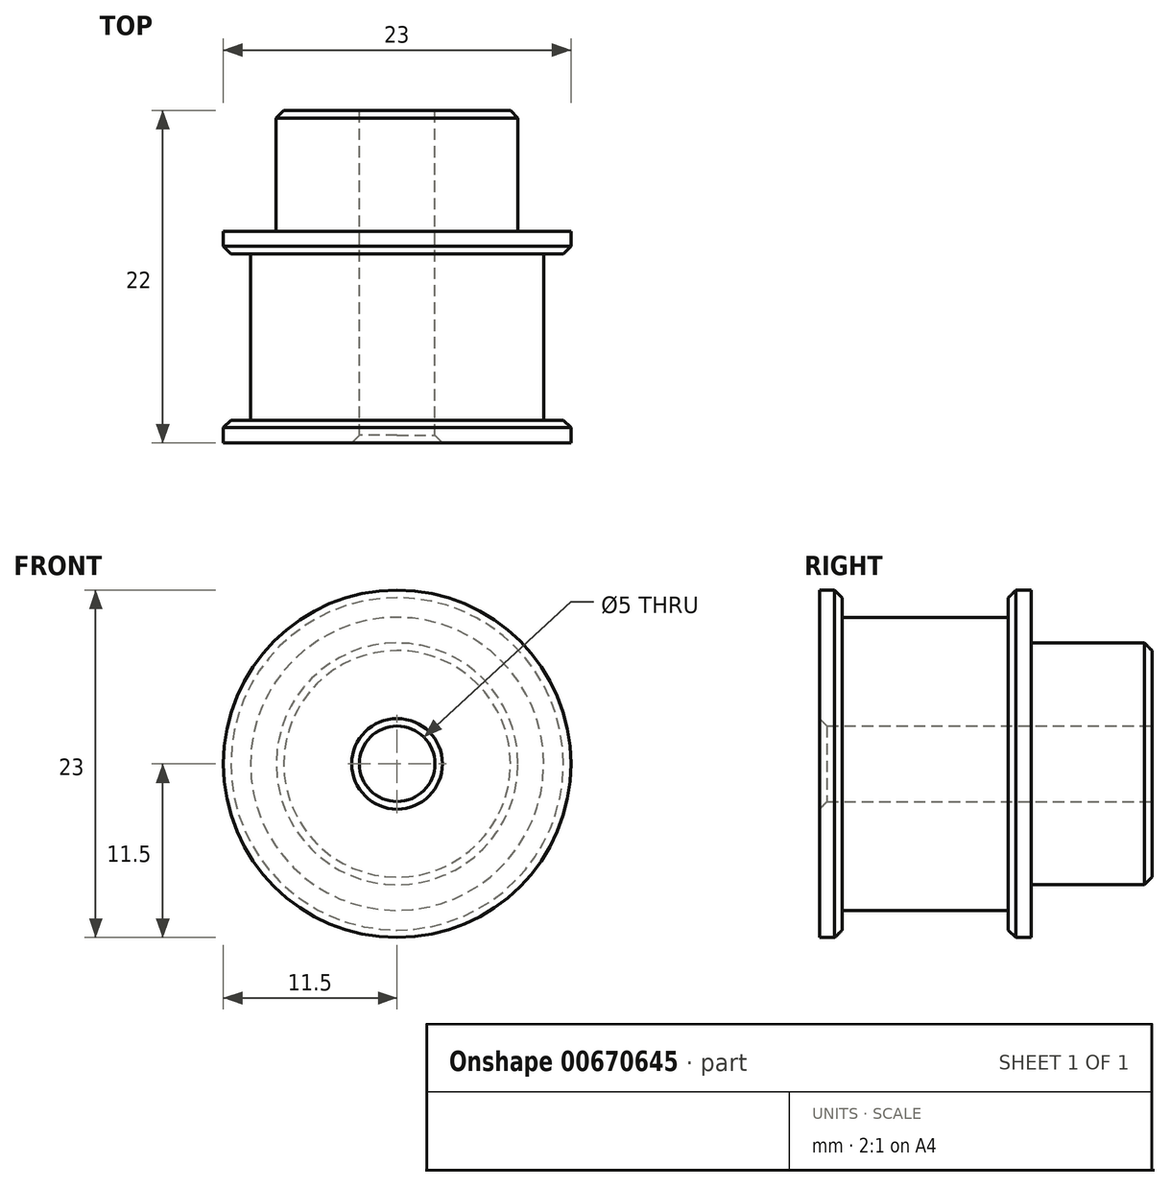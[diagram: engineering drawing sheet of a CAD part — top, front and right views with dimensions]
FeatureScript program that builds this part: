
annotation { "Feature Type Name" : "Feature", "Feature Type Description" : "" }
export const myFeature = defineFeature(function(context is Context, id is Id, definition is map)
    precondition{}
    {
        {
            var Q0;
            Q0=qCreatedBy(makeId("Front.planeOp"),FACE);
            var sketch = newSketch(context, id + "F0", { "sketchPlane" : qUnion([Q0])});
            skCircle(sketch, "E0", {"center": v(0, 0) * mm, "radius": 9.7 * mm});
            skSolve(sketch);
        }
        {
            var Q0;
            Q0=makeQuery(id+"F0.imprint","IMPRINT",FACE,{"disambiguationData":[TD([[makeQuery(id+"F0.imprint","IMPRINT",EDGE,{"derivedFrom":sQuery(id+"F0.wireOp",EDGE,"E0")}),1.0]])]});
            extrude(context, id + "F1", {"entities" : qUnion([Q0]), "endBound" : BoundingType.SYMMETRIC, "depth" : 11 * mm, "offsetDistance" : 25 * mm});
        }
        {
            var Q0;
            Q0=makeQuery(id+"F1.opExtrude","CAP_FACE",FACE,{"disambiguationData":[OSD([sQuery(id+"F0.wireOp",EDGE,"E0")])],"isStart":false});
            var sketch = newSketch(context, id + "F2", { "sketchPlane" : qUnion([Q0])});
            skCircle(sketch, "E1", {"center": v(0, 0) * mm, "radius": 11.5 * mm});
            skSolve(sketch);
        }
        {
            var Q0;
            Q0=qSketchRegion(id+"F2",true);
            extrude(context, id + "F3", {"entities" : qUnion([Q0]), "operationType" : NewBodyOperationType.ADD, "depth" : 1.5 * mm, "offsetDistance" : 25 * mm});
        }
        {
            var Q0;
            Q0=makeQuery(id+"F1.opExtrude","CAP_FACE",FACE,{"disambiguationData":[OSD([sQuery(id+"F0.wireOp",EDGE,"E0")])],"isStart":true});
            var sketch = newSketch(context, id + "F4", { "sketchPlane" : qUnion([Q0])});
            skCircle(sketch, "E2", {"center": v(0, 0) * mm, "radius": 11.5 * mm});
            skSolve(sketch);
        }
        {
            var Q0;
            Q0=qSketchRegion(id+"F4",true);
            extrude(context, id + "F5", {"entities" : qUnion([Q0]), "operationType" : NewBodyOperationType.ADD, "depth" : 1.5 * mm, "offsetDistance" : 25 * mm});
        }
        {
            var Q0;
            Q0=makeQuery(id+"F5.opExtrude","CAP_FACE",FACE,{"disambiguationData":[OSD([sQuery(id+"F4.wireOp",EDGE,"E2")])],"isStart":false});
            var sketch = newSketch(context, id + "F6", { "sketchPlane" : qUnion([Q0])});
            skCircle(sketch, "E3", {"center": v(0, 0) * mm, "radius": 8 * mm});
            skSolve(sketch);
        }
        {
            var Q0;
            Q0=qSketchRegion(id+"F6",true);
            extrude(context, id + "F7", {"entities" : qUnion([Q0]), "operationType" : NewBodyOperationType.ADD, "depth" : 8 * mm, "offsetDistance" : 25 * mm});
        }
        {
            var Q0;
            Q0=makeQuery(id+"F7.opExtrude","CAP_FACE",FACE,{"disambiguationData":[OSD([sQuery(id+"F6.wireOp",EDGE,"E3")])],"isStart":false});
            var sketch = newSketch(context, id + "F8", { "sketchPlane" : qUnion([Q0])});
            skCircle(sketch, "E4", {"center": v(0, 0) * mm, "radius": 2.5 * mm});
            skSolve(sketch);
        }
        {
            var Q0;
            Q0=qSketchRegion(id+"F8",true);
            extrude(context, id + "F9", {"entities" : qUnion([Q0]), "operationType" : NewBodyOperationType.REMOVE, "endBound" : BoundingType.THROUGH_ALL, "oppositeDirection" : true, "depth" : 25 * mm, "offsetDistance" : 25 * mm});
        }
        {
            var Q0;
            Q0=makeQuery(id+"F9.boolean.opBoolean","INTERSECT",EDGE,{"derivedFrom":[makeQuery(id+"F3.opExtrude","CAP_FACE",FACE,{"disambiguationData":[OSD([sQuery(id+"F2.wireOp",EDGE,"E1")])],"isStart":false}),makeQuery(id+"F9.opExtrude","SWEPT_FACE",FACE,{"disambiguationData":[OSD([sQuery(id+"F8.wireOp",EDGE,"E4")])]})]});
            var Q1;
            Q1=makeQuery(id+"F9.boolean.opBoolean","COPY",EDGE,{"derivedFrom":makeQuery(id+"F9.opExtrude","CAP_EDGE",EDGE,{"disambiguationData":[OSD([sQuery(id+"F8.wireOp",EDGE,"E4")])],"isStart":true})});
            var Q2;
            Q2=makeQuery(id+"F3.opExtrude","CAP_EDGE",EDGE,{"disambiguationData":[OSD([sQuery(id+"F2.wireOp",EDGE,"E1")])],"isStart":true});
            var Q3;
            Q3=makeQuery(id+"F5.opExtrude","CAP_EDGE",EDGE,{"disambiguationData":[OSD([sQuery(id+"F4.wireOp",EDGE,"E2")])],"isStart":true});
            var Q4;
            Q4=makeQuery(id+"F7.opExtrude","CAP_EDGE",EDGE,{"disambiguationData":[OSD([sQuery(id+"F6.wireOp",EDGE,"E3")])],"isStart":false});
            chamfer(context, id + "F10", {"entities" : qUnion([Q0, Q1, Q2, Q3, Q4]), "width" : 0.5 * mm, "tangentPropagation" : true});
        }
    });
